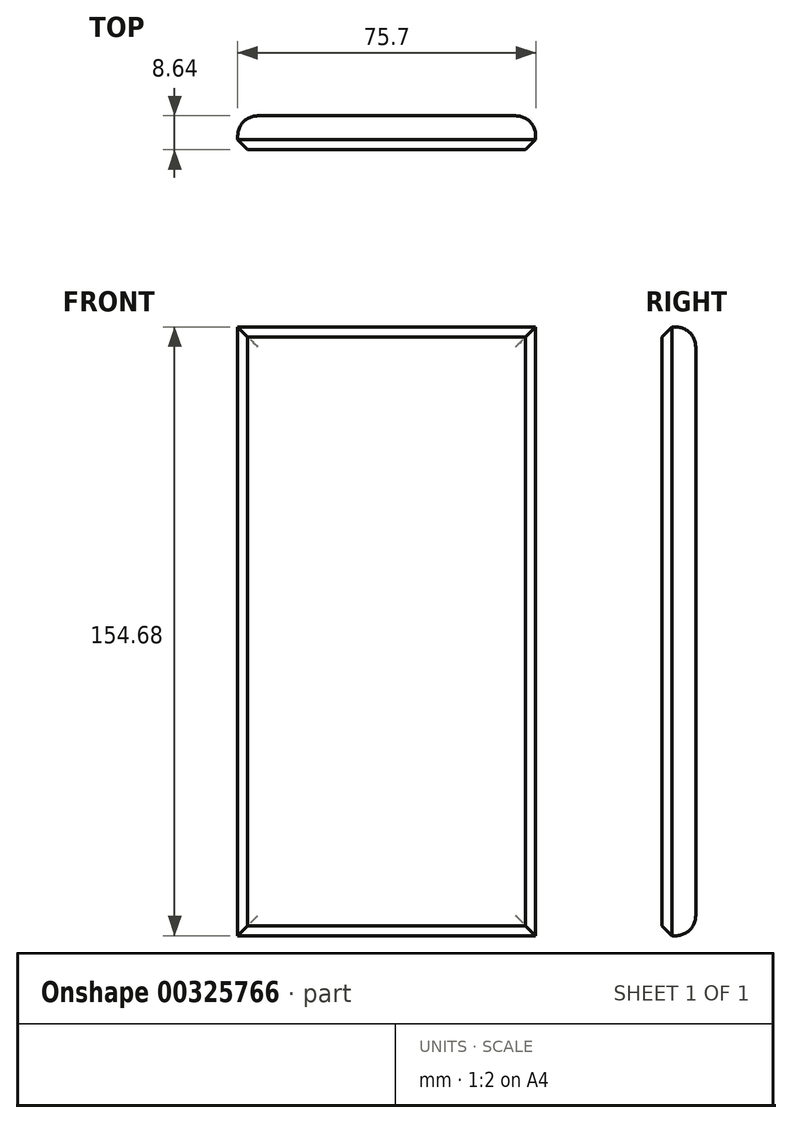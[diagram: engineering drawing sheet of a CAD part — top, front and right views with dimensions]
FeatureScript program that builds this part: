
annotation { "Feature Type Name" : "Feature", "Feature Type Description" : "" }
export const myFeature = defineFeature(function(context is Context, id is Id, definition is map)
    precondition{}
    {
        {
            var Q0;
            Q0=qCreatedBy(makeId("Front.planeOp"),FACE);
            var sketch = newSketch(context, id + "F0", { "sketchPlane" : qUnion([Q0])});
            skLineSegment(sketch, "E0.bottom", {"start": v(-37.85, 77.34) * mm, "end": v(37.85, 77.34) * mm});
            skLineSegment(sketch, "E0.top", {"start": v(-37.85, -77.34) * mm, "end": v(37.85, -77.34) * mm});
            skLineSegment(sketch, "E0.left", {"start": v(-37.85, 77.34) * mm, "end": v(-37.85, -77.34) * mm});
            skLineSegment(sketch, "E0.right", {"start": v(37.85, 77.34) * mm, "end": v(37.85, -77.34) * mm});
            skPoint(sketch, "E0.middle", {"position": v(0, 0) * mm});
            skSolve(sketch);
        }
        {
            var Q0;
            Q0 = qSketchRegion(id + "F0", true);
            extrude(context, id + "F1", {"entities" : qUnion([Q0]), "depth" : 8.64 * mm});
        }
        {
            var Q0;
            Q0=makeQuery(id+"F1.opExtrude","CAP_EDGE",EDGE,{"disambiguationData":[OSD([sQuery(id+"F0.wireOp",EDGE,"E0.right")])],"isStart":true});
            var Q1;
            Q1=makeQuery(id+"F1.opExtrude","CAP_EDGE",EDGE,{"disambiguationData":[OSD([sQuery(id+"F0.wireOp",EDGE,"E0.bottom")])],"isStart":true});
            var Q2;
            Q2=makeQuery(id+"F1.opExtrude","CAP_EDGE",EDGE,{"disambiguationData":[OSD([sQuery(id+"F0.wireOp",EDGE,"E0.left")])],"isStart":true});
            var Q3;
            Q3=makeQuery(id+"F1.opExtrude","CAP_EDGE",EDGE,{"disambiguationData":[OSD([sQuery(id+"F0.wireOp",EDGE,"E0.top")])],"isStart":true});
            fillet(context, id + "F2", {"entities" : qUnion([Q0, Q1, Q2, Q3]), "radius" : 5.08 * mm, "tangentPropagation" : true, "allowEdgeOverflow" : false});
        }
        {
            var Q0;
            Q0=makeQuery(id+"F1.opExtrude","CAP_FACE",FACE,{"disambiguationData":[OSD([sQuery(id+"F0.wireOp",EDGE,"E0.bottom"),sQuery(id+"F0.wireOp",EDGE,"E0.top"),sQuery(id+"F0.wireOp",EDGE,"E0.left"),sQuery(id+"F0.wireOp",EDGE,"E0.right")])],"isStart":false});
            chamfer(context, id + "F3", {"entities" : qUnion([Q0]), "width" : 2.54 * mm, "tangentPropagation" : true});
        }
    });
